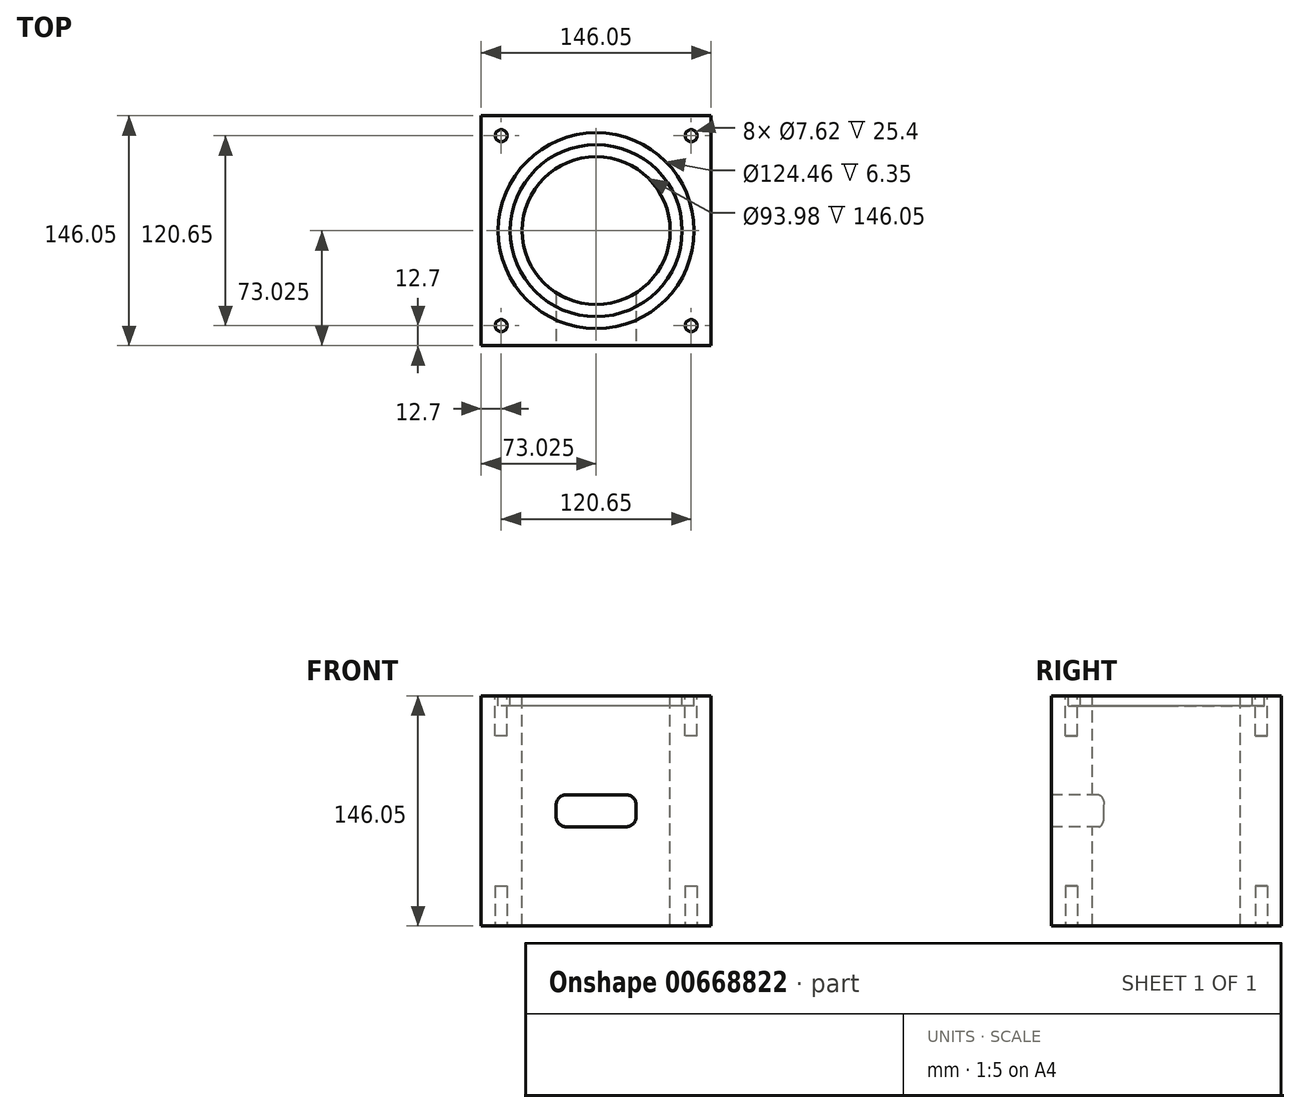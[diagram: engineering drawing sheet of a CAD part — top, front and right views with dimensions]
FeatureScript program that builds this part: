
annotation { "Feature Type Name" : "Feature", "Feature Type Description" : "" }
export const myFeature = defineFeature(function(context is Context, id is Id, definition is map)
    precondition{}
    {
        {
            var Q0;
            Q0=qCreatedBy(makeId("Top.planeOp"),FACE);
            var sketch = newSketch(context, id + "F0", { "sketchPlane" : qUnion([Q0])});
            skLineSegment(sketch, "E0.bottom", {"start": v(76.2, 76.2) * mm, "end": v(-76.2, 76.2) * mm});
            skLineSegment(sketch, "E0.top", {"start": v(76.2, -76.2) * mm, "end": v(-76.2, -76.2) * mm});
            skLineSegment(sketch, "E0.left", {"start": v(76.2, 76.2) * mm, "end": v(76.2, -76.2) * mm});
            skLineSegment(sketch, "E0.right", {"start": v(-76.2, 76.2) * mm, "end": v(-76.2, -76.2) * mm});
            skPoint(sketch, "E0.middle", {"position": v(0, 0) * mm});
            skSolve(sketch);
        }
        {
            var Q0;
            Q0=makeQuery(id+"F0.imprint","IMPRINT",FACE,{"disambiguationData":[TD([[makeQuery(id+"F0.imprint","IMPRINT",EDGE,{"derivedFrom":sQuery(id+"F0.wireOp",EDGE,"E0.bottom")}),1.0]])]});
            extrude(context, id + "F1", {"entities" : qUnion([Q0]), "depth" : 152.4 * mm, "offsetDistance" : 25.4 * mm});
        }
        {
            var Q0;
            Q0=makeQuery(id+"F1.opExtrude","SWEPT_FACE",FACE,{"disambiguationData":[OSD([sQuery(id+"F0.wireOp",EDGE,"E0.top")])]});
            var sketch = newSketch(context, id + "F2", { "sketchPlane" : qUnion([Q0])});
            skLineSegment(sketch, "E1.bottom", {"start": v(76.2, 0) * mm, "end": v(69.85, 0) * mm});
            skLineSegment(sketch, "E1.top", {"start": v(76.2, 152.4) * mm, "end": v(69.85, 152.4) * mm});
            skLineSegment(sketch, "E1.left", {"start": v(76.2, 0) * mm, "end": v(76.2, 152.4) * mm});
            skLineSegment(sketch, "E1.right", {"start": v(69.85, 0) * mm, "end": v(69.85, 152.4) * mm});
            skSolve(sketch);
        }
        {
            var Q0;
            Q0=makeQuery(id+"F2.imprint","IMPRINT",FACE,{"disambiguationData":[TD([[makeQuery(id+"F2.imprint","IMPRINT",EDGE,{"derivedFrom":sQuery(id+"F2.wireOp",EDGE,"E1.bottom")}),-1.0]])]});
            extrude(context, id + "F3", {"entities" : qUnion([Q0]), "operationType" : NewBodyOperationType.REMOVE, "endBound" : BoundingType.THROUGH_ALL, "oppositeDirection" : true, "depth" : 25.4 * mm, "offsetDistance" : 25.4 * mm});
        }
        {
            var Q0;
            Q0=makeQuery(id+"F3.boolean.opBoolean","COPY",FACE,{"derivedFrom":makeQuery(id+"F3.opExtrude","SWEPT_FACE",FACE,{"disambiguationData":[OSD([sQuery(id+"F2.wireOp",EDGE,"E1.right")])]})});
            var sketch = newSketch(context, id + "F4", { "sketchPlane" : qUnion([Q0])});
            skLineSegment(sketch, "E2.bottom", {"start": v(76.2, 0) * mm, "end": v(69.85, 0) * mm});
            skLineSegment(sketch, "E2.top", {"start": v(76.2, 152.4) * mm, "end": v(69.85, 152.4) * mm});
            skLineSegment(sketch, "E2.left", {"start": v(76.2, 0) * mm, "end": v(76.2, 152.4) * mm});
            skLineSegment(sketch, "E2.right", {"start": v(69.85, 0) * mm, "end": v(69.85, 152.4) * mm});
            skSolve(sketch);
        }
        {
            var Q0;
            Q0=makeQuery(id+"F4.imprint","IMPRINT",FACE,{"disambiguationData":[TD([[makeQuery(id+"F4.imprint","IMPRINT",EDGE,{"derivedFrom":sQuery(id+"F4.wireOp",EDGE,"E2.bottom")}),-1.0]])]});
            extrude(context, id + "F5", {"entities" : qUnion([Q0]), "operationType" : NewBodyOperationType.REMOVE, "endBound" : BoundingType.THROUGH_ALL, "oppositeDirection" : true, "depth" : 25.4 * mm, "offsetDistance" : 25.4 * mm});
        }
        {
            var Q0;
            Q0=makeQuery(id+"F1.opExtrude","SWEPT_FACE",FACE,{"disambiguationData":[OSD([sQuery(id+"F0.wireOp",EDGE,"E0.top")])]});
            var sketch = newSketch(context, id + "F6", { "sketchPlane" : qUnion([Q0])});
            skLineSegment(sketch, "E3.bottom", {"start": v(-76.2, 152.4) * mm, "end": v(69.85, 152.4) * mm});
            skLineSegment(sketch, "E3.top", {"start": v(-76.2, 146.05) * mm, "end": v(69.85, 146.05) * mm});
            skLineSegment(sketch, "E3.left", {"start": v(-76.2, 152.4) * mm, "end": v(-76.2, 146.05) * mm});
            skLineSegment(sketch, "E3.right", {"start": v(69.85, 152.4) * mm, "end": v(69.85, 146.05) * mm});
            skSolve(sketch);
        }
        {
            var Q0;
            Q0=makeQuery(id+"F6.imprint","IMPRINT",FACE,{"disambiguationData":[TD([[makeQuery(id+"F6.imprint","IMPRINT",EDGE,{"derivedFrom":sQuery(id+"F6.wireOp",EDGE,"E3.bottom")}),1.0]])]});
            extrude(context, id + "F7", {"entities" : qUnion([Q0]), "operationType" : NewBodyOperationType.REMOVE, "endBound" : BoundingType.THROUGH_ALL, "oppositeDirection" : true, "depth" : 25.4 * mm, "offsetDistance" : 25.4 * mm});
        }
        {
            var Q0;
            Q0=makeQuery(id+"F7.boolean.opBoolean","COPY",FACE,{"derivedFrom":makeQuery(id+"F7.opExtrude","SWEPT_FACE",FACE,{"disambiguationData":[OSD([sQuery(id+"F6.wireOp",EDGE,"E3.top")])]})});
            var sketch = newSketch(context, id + "F8", { "sketchPlane" : qUnion([Q0])});
            skCircle(sketch, "E4", {"center": v(-3.18, -3.18) * mm, "radius": 54.61 * mm});
            skCircle(sketch, "E5.0", {"center": v(-3.18, -3.18) * mm, "radius": 62.23 * mm});
            skCircle(sketch, "E6.0", {"center": v(-3.18, -3.18) * mm, "radius": 47 * mm});
            skCircle(sketch, "E7", {"center": v(-63.5, 57.15) * mm, "radius": 3.81 * mm});
            skPoint(sketch, "E8", {"position": v(-3.18, 69.85) * mm});
            skPoint(sketch, "E9", {"position": v(69.85, -3.18) * mm});
            skCircle(sketch, "E10.1.0", {"center": v(57.15, 57.15) * mm, "radius": 3.81 * mm});
            skCircle(sketch, "E10.2.0", {"center": v(57.15, -63.5) * mm, "radius": 3.81 * mm});
            skCircle(sketch, "E10.3.0", {"center": v(-63.5, -63.5) * mm, "radius": 3.81 * mm});
            skLineSegment(sketch, "E10.anchor1", {"start": v(-3.18, -3.17) * mm, "end": v(-63.5, 57.15) * mm, "construction": true});
            skLineSegment(sketch, "E10.anchor2", {"start": v(-3.18, -3.18) * mm, "end": v(-63.5, -63.5) * mm, "construction": true});
            skSolve(sketch);
        }
        {
            var Q0;
            Q0=makeQuery(id+"F8.imprint","IMPRINT",FACE,{"disambiguationData":[TD([[makeQuery(id+"F8.imprint","IMPRINT",EDGE,{"derivedFrom":sQuery(id+"F8.wireOp",EDGE,"E7")}),1.0]])]});
            var Q1;
            Q1=makeQuery(id+"F8.imprint","IMPRINT",FACE,{"disambiguationData":[TD([[makeQuery(id+"F8.imprint","IMPRINT",EDGE,{"derivedFrom":sQuery(id+"F8.wireOp",EDGE,"E10.1.0")}),1.0]])]});
            var Q2;
            Q2=makeQuery(id+"F8.imprint","IMPRINT",FACE,{"disambiguationData":[TD([[makeQuery(id+"F8.imprint","IMPRINT",EDGE,{"derivedFrom":sQuery(id+"F8.wireOp",EDGE,"E10.2.0")}),1.0]])]});
            var Q3;
            Q3=makeQuery(id+"F8.imprint","IMPRINT",FACE,{"disambiguationData":[TD([[makeQuery(id+"F8.imprint","IMPRINT",EDGE,{"derivedFrom":sQuery(id+"F8.wireOp",EDGE,"E10.3.0")}),1.0]])]});
            extrude(context, id + "F9", {"entities" : qUnion([Q0, Q1, Q2, Q3]), "operationType" : NewBodyOperationType.REMOVE, "oppositeDirection" : true, "depth" : 25.4 * mm, "offsetDistance" : 25.4 * mm});
        }
        {
            var Q0;
            Q0=makeQuery(id+"F8.imprint","IMPRINT",FACE,{"disambiguationData":[TD([[makeQuery(id+"F8.imprint","IMPRINT",EDGE,{"derivedFrom":sQuery(id+"F8.wireOp",EDGE,"E4")}),-1.0]])]});
            extrude(context, id + "F10", {"entities" : qUnion([Q0]), "operationType" : NewBodyOperationType.REMOVE, "oppositeDirection" : true, "depth" : 6.35 * mm, "offsetDistance" : 25.4 * mm});
        }
        {
            var Q0;
            Q0=makeQuery(id+"F8.imprint","IMPRINT",FACE,{"disambiguationData":[TD([[makeQuery(id+"F8.imprint","IMPRINT",EDGE,{"derivedFrom":sQuery(id+"F8.wireOp",EDGE,"E6.0")}),1.0]])]});
            extrude(context, id + "F11", {"entities" : qUnion([Q0]), "operationType" : NewBodyOperationType.REMOVE, "endBound" : BoundingType.THROUGH_ALL, "oppositeDirection" : true, "depth" : 25.4 * mm, "offsetDistance" : 25.4 * mm});
        }
        {
            var Q0;
            Q0=makeQuery(id+"F1.opExtrude","SWEPT_FACE",FACE,{"disambiguationData":[OSD([sQuery(id+"F0.wireOp",EDGE,"E0.top")])]});
            var sketch = newSketch(context, id + "F12", { "sketchPlane" : qUnion([Q0])});
            skLineSegment(sketch, "E11.bottom", {"start": v(15.87, 83.19) * mm, "end": v(-22.23, 83.19) * mm});
            skLineSegment(sketch, "E11.top", {"start": v(15.87, 62.87) * mm, "end": v(-22.23, 62.87) * mm});
            skLineSegment(sketch, "E11.left", {"start": v(22.23, 76.83) * mm, "end": v(22.23, 69.22) * mm});
            skLineSegment(sketch, "E11.right", {"start": v(-28.57, 76.84) * mm, "end": v(-28.57, 69.22) * mm});
            skLineSegment(sketch, "E12.0.0", {"start": v(69.85, 146.05) * mm, "end": v(-76.2, 146.05) * mm});
            skLineSegment(sketch, "E12.0.1", {"start": v(-76.2, 146.05) * mm, "end": v(-76.2, 0) * mm});
            skLineSegment(sketch, "E12.0.2", {"start": v(-76.2, 0) * mm, "end": v(69.85, 0) * mm});
            skLineSegment(sketch, "E12.0.3", {"start": v(69.85, 0) * mm, "end": v(69.85, 146.05) * mm});
            skPoint(sketch, "E13", {"position": v(-3.18, 62.87) * mm});
            skPoint(sketch, "E14", {"position": v(22.23, 73.03) * mm});
            skPoint(sketch, "E15", {"position": v(69.85, 73.03) * mm});
            skPoint(sketch, "E16", {"position": v(-3.17, 0) * mm});
            skPoint(sketch, "E17.visualSharp", {"position": v(-28.57, 62.87) * mm});
            skArc(sketch, "E17.filletArc", {"start": v(-28.58, 69.22) * mm, "mid": v(-26.72, 64.72) * mm, "end": v(-22.23, 62.87) * mm});
            skPoint(sketch, "E18.visualSharp", {"position": v(-28.57, 83.19) * mm});
            skArc(sketch, "E18.filletArc", {"start": v(-22.23, 83.19) * mm, "mid": v(-26.72, 81.33) * mm, "end": v(-28.58, 76.84) * mm});
            skPoint(sketch, "E19.visualSharp", {"position": v(22.23, 83.19) * mm});
            skArc(sketch, "E19.filletArc", {"start": v(22.23, 76.83) * mm, "mid": v(20.37, 81.33) * mm, "end": v(15.87, 83.19) * mm});
            skPoint(sketch, "E20.visualSharp", {"position": v(22.23, 62.87) * mm});
            skArc(sketch, "E20.filletArc", {"start": v(15.87, 62.87) * mm, "mid": v(20.37, 64.72) * mm, "end": v(22.23, 69.22) * mm});
            skSolve(sketch);
        }
        {
            var Q0;
            Q0=makeQuery(id+"F12.imprint","IMPRINT",FACE,{"disambiguationData":[TD([[makeQuery(id+"F12.imprint","IMPRINT",EDGE,{"derivedFrom":sQuery(id+"F12.wireOp",EDGE,"E11.bottom")}),1.0]])]});
            extrude(context, id + "F13", {"entities" : qUnion([Q0]), "operationType" : NewBodyOperationType.REMOVE, "oppositeDirection" : true, "depth" : 50.8 * mm, "offsetDistance" : 25.4 * mm});
        }
        {
            var Q0;
            Q0=makeQuery(id+"F1.opExtrude","CAP_FACE",FACE,{"disambiguationData":[OSD([sQuery(id+"F0.wireOp",EDGE,"E0.bottom"),sQuery(id+"F0.wireOp",EDGE,"E0.top"),sQuery(id+"F0.wireOp",EDGE,"E0.left"),sQuery(id+"F0.wireOp",EDGE,"E0.right")])],"isStart":true});
            var sketch = newSketch(context, id + "F14", { "sketchPlane" : qUnion([Q0])});
            skPoint(sketch, "E21.0", {"position": v(-63.5, 63.5) * mm});
            skCircle(sketch, "E22", {"center": v(-63.5, 63.5) * mm, "radius": 3.81 * mm});
            skPoint(sketch, "E23.0", {"position": v(-3.18, 3.18) * mm});
            skCircle(sketch, "E24.1.0", {"center": v(-63.5, -57.15) * mm, "radius": 3.81 * mm});
            skCircle(sketch, "E24.2.0", {"center": v(57.15, -57.15) * mm, "radius": 3.81 * mm});
            skCircle(sketch, "E24.3.0", {"center": v(57.15, 63.5) * mm, "radius": 3.81 * mm});
            skSolve(sketch);
        }
        {
            var Q0;
            Q0=makeQuery(id+"F14.imprint","IMPRINT",FACE,{"disambiguationData":[TD([[makeQuery(id+"F14.imprint","IMPRINT",EDGE,{"derivedFrom":sQuery(id+"F14.wireOp",EDGE,"E22")}),1.0]])]});
            var Q1;
            Q1=makeQuery(id+"F14.imprint","IMPRINT",FACE,{"disambiguationData":[TD([[makeQuery(id+"F14.imprint","IMPRINT",EDGE,{"derivedFrom":sQuery(id+"F14.wireOp",EDGE,"E24.3.0")}),1.0]])]});
            var Q2;
            Q2=makeQuery(id+"F14.imprint","IMPRINT",FACE,{"disambiguationData":[TD([[makeQuery(id+"F14.imprint","IMPRINT",EDGE,{"derivedFrom":sQuery(id+"F14.wireOp",EDGE,"E24.2.0")}),1.0]])]});
            var Q3;
            Q3=makeQuery(id+"F14.imprint","IMPRINT",FACE,{"disambiguationData":[TD([[makeQuery(id+"F14.imprint","IMPRINT",EDGE,{"derivedFrom":sQuery(id+"F14.wireOp",EDGE,"E24.1.0")}),1.0]])]});
            extrude(context, id + "F15", {"entities" : qUnion([Q0, Q1, Q2, Q3]), "operationType" : NewBodyOperationType.REMOVE, "oppositeDirection" : true, "depth" : 25.4 * mm, "offsetDistance" : 25.4 * mm});
        }
    });
